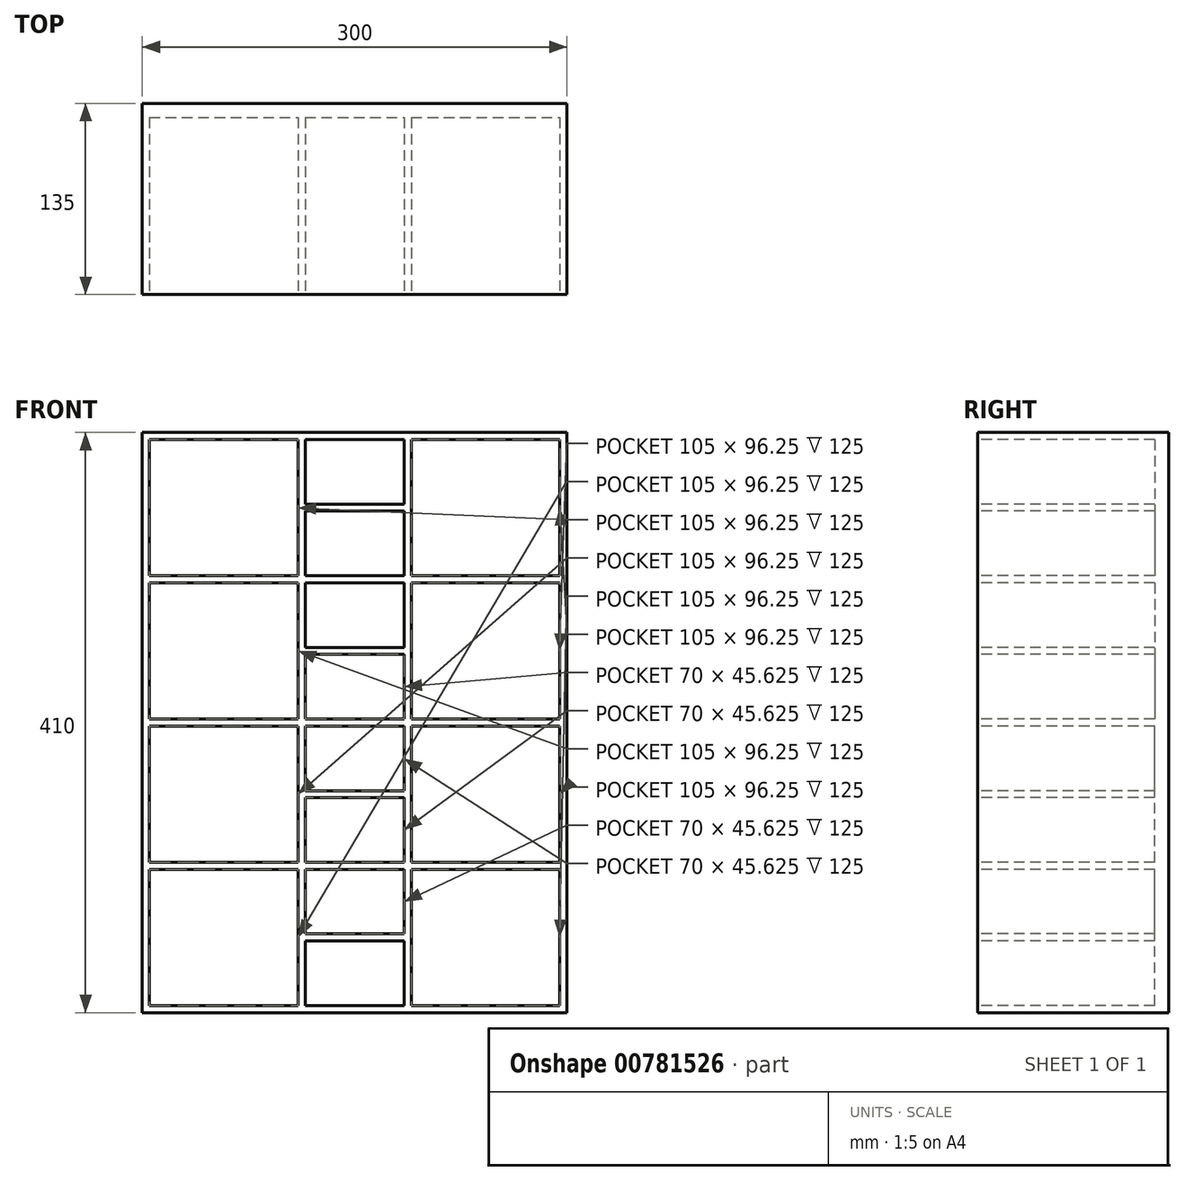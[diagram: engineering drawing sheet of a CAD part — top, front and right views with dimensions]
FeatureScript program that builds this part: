
annotation { "Feature Type Name" : "Feature", "Feature Type Description" : "" }
export const myFeature = defineFeature(function(context is Context, id is Id, definition is map)
    precondition{}
    {
        {
            var Q0;
            Q0=qCreatedBy(makeId("Top.planeOp"),FACE);
            var sketch = newSketch(context, id + "F0", { "sketchPlane" : qUnion([Q0])});
            skLineSegment(sketch, "E0.bottom", {"start": v(0, 0) * mm, "end": v(300, 0) * mm});
            skLineSegment(sketch, "E0.top", {"start": v(0, 135) * mm, "end": v(300, 135) * mm});
            skLineSegment(sketch, "E0.left", {"start": v(0, 0) * mm, "end": v(0, 135) * mm});
            skLineSegment(sketch, "E0.right", {"start": v(300, 0) * mm, "end": v(300, 135) * mm});
            skSolve(sketch);
        }
        {
            var Q0;
            Q0=makeQuery(id+"F0.imprint","IMPRINT",FACE,{"disambiguationData":[TD([[makeQuery(id+"F0.imprint","IMPRINT",EDGE,{"derivedFrom":sQuery(id+"F0.wireOp",EDGE,"E0.bottom")}),1.0]])]});
            extrude(context, id + "F1", {"entities" : qUnion([Q0]), "depth" : 410 * mm, "offsetDistance" : 25 * mm});
        }
        {
            var Q0;
            Q0=makeQuery(id+"F1.opExtrude","SWEPT_FACE",FACE,{"disambiguationData":[OSD([sQuery(id+"F0.wireOp",EDGE,"E0.bottom")])]});
            var sketch = newSketch(context, id + "F2", { "sketchPlane" : qUnion([Q0])});
            skLineSegment(sketch, "E1.bottom", {"start": v(5, 405) * mm, "end": v(110, 405) * mm});
            skLineSegment(sketch, "E1.top", {"start": v(5, 308.75) * mm, "end": v(110, 308.75) * mm});
            skLineSegment(sketch, "E1.left", {"start": v(5, 405) * mm, "end": v(5, 308.75) * mm});
            skLineSegment(sketch, "E1.right", {"start": v(110, 405) * mm, "end": v(110, 308.75) * mm});
            skLineSegment(sketch, "E2.bottom", {"start": v(5, 303.75) * mm, "end": v(110, 303.75) * mm});
            skLineSegment(sketch, "E2.top", {"start": v(5, 207.5) * mm, "end": v(110, 207.5) * mm});
            skLineSegment(sketch, "E2.left", {"start": v(5, 303.75) * mm, "end": v(5, 207.5) * mm});
            skLineSegment(sketch, "E2.right", {"start": v(110, 303.75) * mm, "end": v(110, 207.5) * mm});
            skLineSegment(sketch, "E3.bottom", {"start": v(190, 405) * mm, "end": v(295, 405) * mm});
            skLineSegment(sketch, "E3.top", {"start": v(190, 308.75) * mm, "end": v(295, 308.75) * mm});
            skLineSegment(sketch, "E3.left", {"start": v(190, 405) * mm, "end": v(190, 308.75) * mm});
            skLineSegment(sketch, "E3.right", {"start": v(295, 405) * mm, "end": v(295, 308.75) * mm});
            skLineSegment(sketch, "E4.bottom", {"start": v(190, 303.75) * mm, "end": v(295, 303.75) * mm});
            skLineSegment(sketch, "E4.top", {"start": v(190, 207.5) * mm, "end": v(295, 207.5) * mm});
            skLineSegment(sketch, "E4.left", {"start": v(190, 303.75) * mm, "end": v(190, 207.5) * mm});
            skLineSegment(sketch, "E4.right", {"start": v(295, 303.75) * mm, "end": v(295, 207.5) * mm});
            skLineSegment(sketch, "E5", {"start": v(0, 205) * mm, "end": v(300, 205) * mm, "construction": true});
            skLineSegment(sketch, "E6.bottom", {"start": v(115, 405) * mm, "end": v(185, 405) * mm});
            skLineSegment(sketch, "E6.top", {"start": v(115, 359.38) * mm, "end": v(185, 359.38) * mm});
            skLineSegment(sketch, "E6.left", {"start": v(115, 405) * mm, "end": v(115, 359.38) * mm});
            skLineSegment(sketch, "E6.right", {"start": v(185, 405) * mm, "end": v(185, 359.38) * mm});
            skLineSegment(sketch, "E7.bottom", {"start": v(115, 354.38) * mm, "end": v(185, 354.38) * mm});
            skLineSegment(sketch, "E7.top", {"start": v(115, 308.75) * mm, "end": v(185, 308.75) * mm});
            skLineSegment(sketch, "E7.left", {"start": v(115, 354.38) * mm, "end": v(115, 308.75) * mm});
            skLineSegment(sketch, "E7.right", {"start": v(185, 354.38) * mm, "end": v(185, 308.75) * mm});
            skLineSegment(sketch, "E8.bottom", {"start": v(115, 303.75) * mm, "end": v(185, 303.75) * mm});
            skLineSegment(sketch, "E8.top", {"start": v(115, 258.12) * mm, "end": v(185, 258.12) * mm});
            skLineSegment(sketch, "E8.left", {"start": v(115, 303.75) * mm, "end": v(115, 258.12) * mm});
            skLineSegment(sketch, "E8.right", {"start": v(185, 303.75) * mm, "end": v(185, 258.12) * mm});
            skLineSegment(sketch, "E9", {"start": v(5, 308.75) * mm, "end": v(5, 303.75) * mm});
            skLineSegment(sketch, "E10", {"start": v(110, 405) * mm, "end": v(115, 405) * mm});
            skLineSegment(sketch, "E11", {"start": v(185, 405) * mm, "end": v(190, 405) * mm});
            skLineSegment(sketch, "E12", {"start": v(115, 359.38) * mm, "end": v(115, 354.38) * mm});
            skLineSegment(sketch, "E13", {"start": v(115, 308.75) * mm, "end": v(115, 303.75) * mm});
            skLineSegment(sketch, "E14", {"start": v(5, 405) * mm, "end": v(0, 405) * mm});
            skLineSegment(sketch, "E15", {"start": v(5, 410) * mm, "end": v(5, 405) * mm});
            skLineSegment(sketch, "E16", {"start": v(295, 405) * mm, "end": v(300, 405) * mm});
            skLineSegment(sketch, "E17.bottom", {"start": v(115, 253.13) * mm, "end": v(185, 253.13) * mm});
            skLineSegment(sketch, "E17.top", {"start": v(115, 207.5) * mm, "end": v(185, 207.5) * mm});
            skLineSegment(sketch, "E17.left", {"start": v(115, 253.13) * mm, "end": v(115, 207.5) * mm});
            skLineSegment(sketch, "E17.right", {"start": v(185, 253.13) * mm, "end": v(185, 207.5) * mm});
            skLineSegment(sketch, "E18", {"start": v(115, 258.12) * mm, "end": v(115, 253.13) * mm});
            skLineSegment(sketch, "E19.MirrorCS", {"start": v(185, 106.25) * mm, "end": v(185, 151.88) * mm});
            skLineSegment(sketch, "E20.MirrorCS", {"start": v(295, 5) * mm, "end": v(300, 5) * mm});
            skLineSegment(sketch, "E21.MirrorCS", {"start": v(5, 0) * mm, "end": v(5, 5) * mm});
            skLineSegment(sketch, "E22.MirrorCS", {"start": v(5, 5) * mm, "end": v(0, 5) * mm});
            skLineSegment(sketch, "E23.MirrorCS", {"start": v(115, 156.88) * mm, "end": v(115, 202.5) * mm});
            skLineSegment(sketch, "E24.MirrorCS", {"start": v(115, 55.62) * mm, "end": v(115, 101.25) * mm});
            skLineSegment(sketch, "E25.MirrorCS", {"start": v(185, 5) * mm, "end": v(185, 50.63) * mm});
            skLineSegment(sketch, "E26.MirrorCS", {"start": v(115, 5) * mm, "end": v(115, 50.63) * mm});
            skLineSegment(sketch, "E27.MirrorCS", {"start": v(115, 151.87) * mm, "end": v(185, 151.87) * mm});
            skLineSegment(sketch, "E28.MirrorCS", {"start": v(115, 50.62) * mm, "end": v(185, 50.62) * mm});
            skLineSegment(sketch, "E29.MirrorCS", {"start": v(190, 106.25) * mm, "end": v(190, 202.5) * mm});
            skLineSegment(sketch, "E30.MirrorCS", {"start": v(295, 106.25) * mm, "end": v(295, 202.5) * mm});
            skLineSegment(sketch, "E31.MirrorCS", {"start": v(5, 5) * mm, "end": v(110, 5) * mm});
            skLineSegment(sketch, "E32.MirrorCS", {"start": v(5, 101.25) * mm, "end": v(110, 101.25) * mm});
            skLineSegment(sketch, "E33.MirrorCS", {"start": v(5, 5) * mm, "end": v(5, 101.25) * mm});
            skLineSegment(sketch, "E34.MirrorCS", {"start": v(190, 202.5) * mm, "end": v(295, 202.5) * mm});
            skLineSegment(sketch, "E35.MirrorCS", {"start": v(115, 202.5) * mm, "end": v(185, 202.5) * mm});
            skLineSegment(sketch, "E36.MirrorCS", {"start": v(115, 101.25) * mm, "end": v(185, 101.25) * mm});
            skLineSegment(sketch, "E37.MirrorCS", {"start": v(115, 156.88) * mm, "end": v(185, 156.88) * mm});
            skLineSegment(sketch, "E38.MirrorCS", {"start": v(185, 156.88) * mm, "end": v(185, 202.5) * mm});
            skLineSegment(sketch, "E39.MirrorCS", {"start": v(185, 55.62) * mm, "end": v(185, 101.25) * mm});
            skLineSegment(sketch, "E40.MirrorCS", {"start": v(110, 5) * mm, "end": v(110, 101.25) * mm});
            skLineSegment(sketch, "E41.MirrorCS", {"start": v(115, 55.62) * mm, "end": v(185, 55.62) * mm});
            skLineSegment(sketch, "E42.MirrorCS", {"start": v(190, 101.25) * mm, "end": v(295, 101.25) * mm});
            skLineSegment(sketch, "E43.MirrorCS", {"start": v(5, 106.25) * mm, "end": v(110, 106.25) * mm});
            skLineSegment(sketch, "E44.MirrorCS", {"start": v(5, 202.5) * mm, "end": v(110, 202.5) * mm});
            skLineSegment(sketch, "E45.MirrorCS", {"start": v(5, 106.25) * mm, "end": v(5, 202.5) * mm});
            skLineSegment(sketch, "E46.MirrorCS", {"start": v(190, 106.25) * mm, "end": v(295, 106.25) * mm});
            skLineSegment(sketch, "E47.MirrorCS", {"start": v(190, 5) * mm, "end": v(295, 5) * mm});
            skLineSegment(sketch, "E48.MirrorCS", {"start": v(115, 5) * mm, "end": v(185, 5) * mm});
            skLineSegment(sketch, "E49.MirrorCS", {"start": v(190, 5) * mm, "end": v(190, 101.25) * mm});
            skLineSegment(sketch, "E50.MirrorCS", {"start": v(115, 106.25) * mm, "end": v(185, 106.25) * mm});
            skLineSegment(sketch, "E51.MirrorCS", {"start": v(110, 106.25) * mm, "end": v(110, 202.5) * mm});
            skLineSegment(sketch, "E52.MirrorCS", {"start": v(295, 5) * mm, "end": v(295, 101.25) * mm});
            skLineSegment(sketch, "E53.MirrorCS", {"start": v(115, 106.25) * mm, "end": v(115, 151.88) * mm});
            skLineSegment(sketch, "E54.MirrorCS", {"start": v(5, 101.25) * mm, "end": v(5, 106.25) * mm});
            skLineSegment(sketch, "E55.MirrorCS", {"start": v(115, 50.63) * mm, "end": v(115, 55.62) * mm});
            skLineSegment(sketch, "E56.MirrorCS", {"start": v(185, 5) * mm, "end": v(190, 5) * mm});
            skLineSegment(sketch, "E57.MirrorCS", {"start": v(110, 5) * mm, "end": v(115, 5) * mm});
            skLineSegment(sketch, "E58.MirrorCS", {"start": v(115, 151.88) * mm, "end": v(115, 156.88) * mm});
            skLineSegment(sketch, "E59.MirrorCS", {"start": v(115, 101.25) * mm, "end": v(115, 106.25) * mm});
            skLineSegment(sketch, "E60", {"start": v(5, 202.5) * mm, "end": v(5, 207.5) * mm});
            skSolve(sketch);
        }
        {
            var Q0;
            Q0 = qSketchRegion(id + "F2", true);
            extrude(context, id + "F3", {"entities" : qUnion([Q0]), "operationType" : NewBodyOperationType.REMOVE, "oppositeDirection" : true, "depth" : 125 * mm, "offsetDistance" : 25 * mm});
        }
    });
